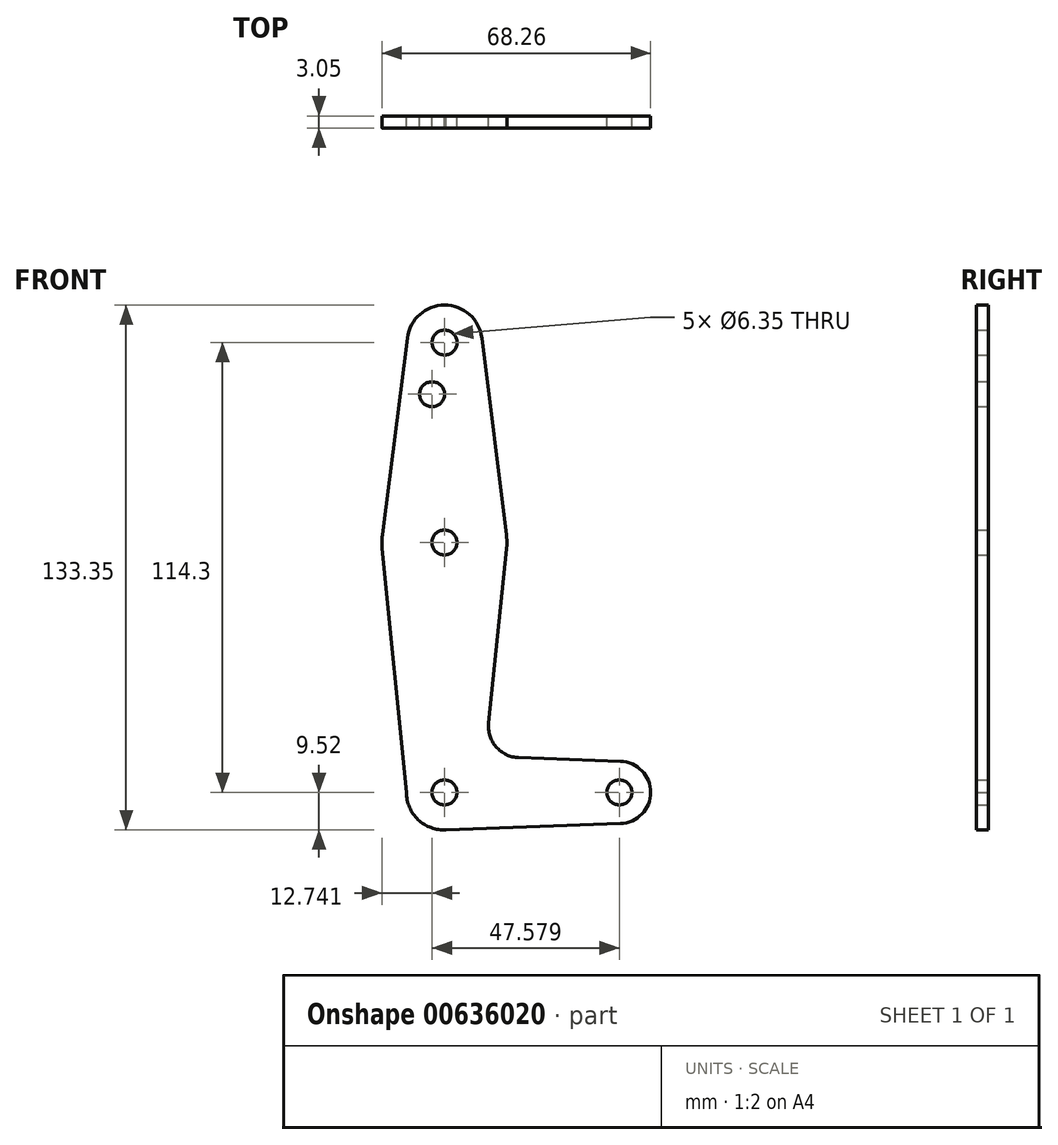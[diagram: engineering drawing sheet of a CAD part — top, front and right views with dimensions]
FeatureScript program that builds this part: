
annotation { "Feature Type Name" : "Feature", "Feature Type Description" : "" }
export const myFeature = defineFeature(function(context is Context, id is Id, definition is map)
    precondition{}
    {
        {
            var Q0;
            Q0=qCreatedBy(makeId("Front.planeOp"),FACE);
            var sketch = newSketch(context, id + "F0", { "sketchPlane" : qUnion([Q0])});
            skCircle(sketch, "E0", {"center": v(-0.11, 0) * mm, "radius": 9.53 * mm});
            skCircle(sketch, "E1", {"center": v(0, 63.5) * mm, "radius": 15.88 * mm});
            skCircle(sketch, "E2", {"center": v(0.05, 114.3) * mm, "radius": 9.53 * mm});
            skLineSegment(sketch, "E3", {"start": v(0, 0) * mm, "end": v(44.45, 0) * mm, "construction": true});
            skCircle(sketch, "E4", {"center": v(44.45, 0) * mm, "radius": 7.94 * mm});
            skLineSegment(sketch, "E5", {"start": v(0.05, 114.3) * mm, "end": v(0, 0) * mm, "construction": true});
            skLineSegment(sketch, "E6", {"start": v(-9.4, 115.5) * mm, "end": v(-15.75, 65.5) * mm});
            skLineSegment(sketch, "E7", {"start": v(9.5, 115.48) * mm, "end": v(15.75, 65.47) * mm});
            skLineSegment(sketch, "E8", {"start": v(-9.64, 0) * mm, "end": v(-15.8, 61.93) * mm});
            skLineSegment(sketch, "E9", {"start": v(11.23, 17.61) * mm, "end": v(15.8, 61.87) * mm});
            skLineSegment(sketch, "E10", {"start": v(18.85, 8.85) * mm, "end": v(44.73, 7.93) * mm});
            skLineSegment(sketch, "E11", {"start": v(0, -9.52) * mm, "end": v(44.73, -7.93) * mm});
            skCircle(sketch, "E12", {"center": v(-3.13, 101.17) * mm, "radius": 3.17 * mm});
            skCircle(sketch, "E13", {"center": v(0.05, 114.3) * mm, "radius": 3.17 * mm});
            skCircle(sketch, "E14", {"center": v(0, 63.5) * mm, "radius": 3.18 * mm});
            skCircle(sketch, "E15", {"center": v(0, 0) * mm, "radius": 3.18 * mm});
            skCircle(sketch, "E16", {"center": v(44.45, 0) * mm, "radius": 3.17 * mm});
            skArc(sketch, "E17.filletArc", {"start": v(11.23, 17.61) * mm, "mid": v(13.14, 11.58) * mm, "end": v(18.85, 8.85) * mm});
            skSolve(sketch);
        }
        {
            var Q0;
            Q0=qSketchRegion(id+"F0",true);
            extrude(context, id + "F1", {"entities" : qUnion([Q0]), "depth" : 3.05 * mm});
        }
    });
